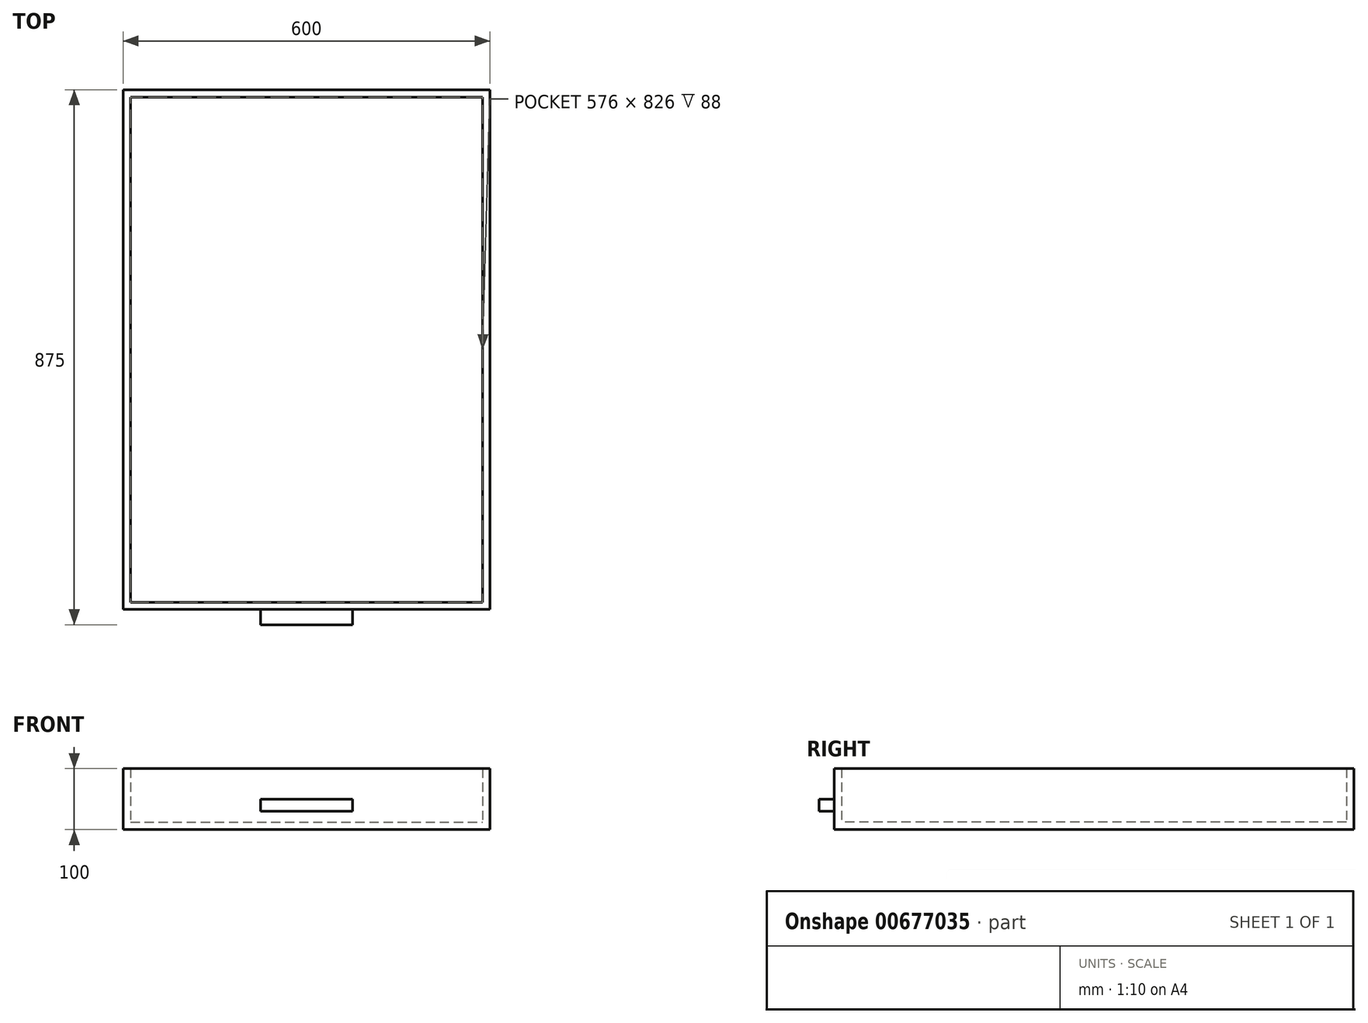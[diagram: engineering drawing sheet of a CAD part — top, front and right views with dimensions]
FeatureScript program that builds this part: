
annotation { "Feature Type Name" : "Feature", "Feature Type Description" : "" }
export const myFeature = defineFeature(function(context is Context, id is Id, definition is map)
    precondition{}
    {
        {
            var Q0;
            Q0=qCreatedBy(makeId("Top.planeOp"),FACE);
            var sketch = newSketch(context, id + "F0", { "sketchPlane" : qUnion([Q0])});
            skLineSegment(sketch, "E0.bottom", {"start": v(0, 0) * mm, "end": v(600, 0) * mm});
            skLineSegment(sketch, "E0.top", {"start": v(0, -850) * mm, "end": v(600, -850) * mm});
            skLineSegment(sketch, "E0.left", {"start": v(0, 0) * mm, "end": v(0, -850) * mm});
            skLineSegment(sketch, "E0.right", {"start": v(600, 0) * mm, "end": v(600, -850) * mm});
            skSolve(sketch);
        }
        {
            var Q0;
            Q0=makeQuery(id+"F0.imprint","IMPRINT",FACE,{"disambiguationData":[TD([[makeQuery(id+"F0.imprint","IMPRINT",EDGE,{"derivedFrom":sQuery(id+"F0.wireOp",EDGE,"E0.bottom")}),-1.0]])]});
            extrude(context, id + "F1", {"entities" : qUnion([Q0]), "depth" : 12 * mm, "offsetDistance" : 25 * mm});
        }
        {
            var Q0;
            Q0=makeQuery(id+"F1.opExtrude","CAP_FACE",FACE,{"disambiguationData":[OSD([sQuery(id+"F0.wireOp",EDGE,"E0.bottom"),sQuery(id+"F0.wireOp",EDGE,"E0.top"),sQuery(id+"F0.wireOp",EDGE,"E0.left"),sQuery(id+"F0.wireOp",EDGE,"E0.right")])],"isStart":false});
            var sketch = newSketch(context, id + "F2", { "sketchPlane" : qUnion([Q0])});
            skLineSegment(sketch, "E1.bottom", {"start": v(0, 0) * mm, "end": v(600, 0) * mm});
            skLineSegment(sketch, "E1.top", {"start": v(0, -850) * mm, "end": v(600, -850) * mm});
            skLineSegment(sketch, "E1.left", {"start": v(0, 0) * mm, "end": v(0, -850) * mm});
            skLineSegment(sketch, "E1.right", {"start": v(600, 0) * mm, "end": v(600, -850) * mm});
            skLineSegment(sketch, "E2.0", {"start": v(12, -12) * mm, "end": v(12, -838) * mm});
            skLineSegment(sketch, "E2.1", {"start": v(12, -12) * mm, "end": v(588, -12) * mm});
            skLineSegment(sketch, "E2.2", {"start": v(588, -12) * mm, "end": v(588, -838) * mm});
            skLineSegment(sketch, "E2.3", {"start": v(12, -838) * mm, "end": v(588, -838) * mm});
            skSolve(sketch);
        }
        {
            var Q0;
            Q0 = qSketchRegion(id + "F2", true);
            extrude(context, id + "F3", {"entities" : qUnion([Q0]), "operationType" : NewBodyOperationType.ADD, "depth" : 88 * mm, "offsetDistance" : 25 * mm});
        }
        {
            var Q0;
            Q0=makeQuery(id+"F3.boolean.opBoolean","MERGE",FACE,{"derivedFrom":[makeQuery(id+"F1.opExtrude","SWEPT_FACE",FACE,{"disambiguationData":[OSD([sQuery(id+"F0.wireOp",EDGE,"E0.top")])]}),makeQuery(id+"F3.opExtrude","SWEPT_FACE",FACE,{"disambiguationData":[OSD([sQuery(id+"F2.wireOp",EDGE,"E1.top")])]})]});
            var sketch = newSketch(context, id + "F4", { "sketchPlane" : qUnion([Q0])});
            skLineSegment(sketch, "E3.bottom", {"start": v(225, 50) * mm, "end": v(375, 50) * mm});
            skLineSegment(sketch, "E3.top", {"start": v(225, 30) * mm, "end": v(375, 30) * mm});
            skLineSegment(sketch, "E3.left", {"start": v(225, 50) * mm, "end": v(225, 30) * mm});
            skLineSegment(sketch, "E3.right", {"start": v(375, 50) * mm, "end": v(375, 30) * mm});
            skSolve(sketch);
        }
        {
            var Q0;
            Q0=makeQuery(id+"F4.imprint","IMPRINT",FACE,{"disambiguationData":[TD([[makeQuery(id+"F4.imprint","IMPRINT",EDGE,{"derivedFrom":sQuery(id+"F4.wireOp",EDGE,"E3.bottom")}),-1.0]])]});
            extrude(context, id + "F5", {"entities" : qUnion([Q0]), "operationType" : NewBodyOperationType.ADD, "depth" : 25 * mm, "offsetDistance" : 25 * mm});
        }
    });
